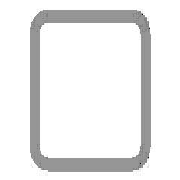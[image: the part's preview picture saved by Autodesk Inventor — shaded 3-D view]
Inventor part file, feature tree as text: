
AUTODESK INVENTOR PART (.ipt)
format: ipt  version: 2024 (Build 280153000, 153)  size: 164,352 bytes
history: native  units: mm (DEFAULTED — no unit token found)
features: plane x5, other x4, split x4, extrude x1, sketch x1
ambient origin geometry x8: Origin, YZ Plane, XZ Plane, XY Plane, X Axis, Y Axis, Z Axis, Center Point
bodies: Solid1 (feature_tree)
feature tree (15):
  parser-record x1  (decoder bookkeeping rows leaked as tree rows — omitted from the tree; the rows remain in map.json)
  other  "Driven Length"
  other  "Plano inicial"
  other  "Plano final"
  extrude  "Cuerpo"  TaperAngle=0.0deg  [1 undecoded]
  plane  "Plano de trabajo4"
  split  "Dividir1"
  plane  "Plano de trabajo5"
  split  "Dividir2"
  plane  "Plano de trabajo6"
  split  "Dividir3"
  plane  "Plano de trabajo7"
  split  "Dividir4"
  sketch  "Sketch3"  dims[d3=847.080256mm d4=0.0mm d10=50.8mm d11=50.8mm d12=3.175mm d13=-23.540128mm d14=823.540128mm d15=25.4mm d16=25.4mm d17=6.35mm d18=90.0deg d19=847.080256mm]
  plane  "Work Plane3"
note: 1 required parameter value undecoded (feature->parameter linkage not recoverable at this tier; creation-order binding heuristic only, values carry confidence <= 0.55)
